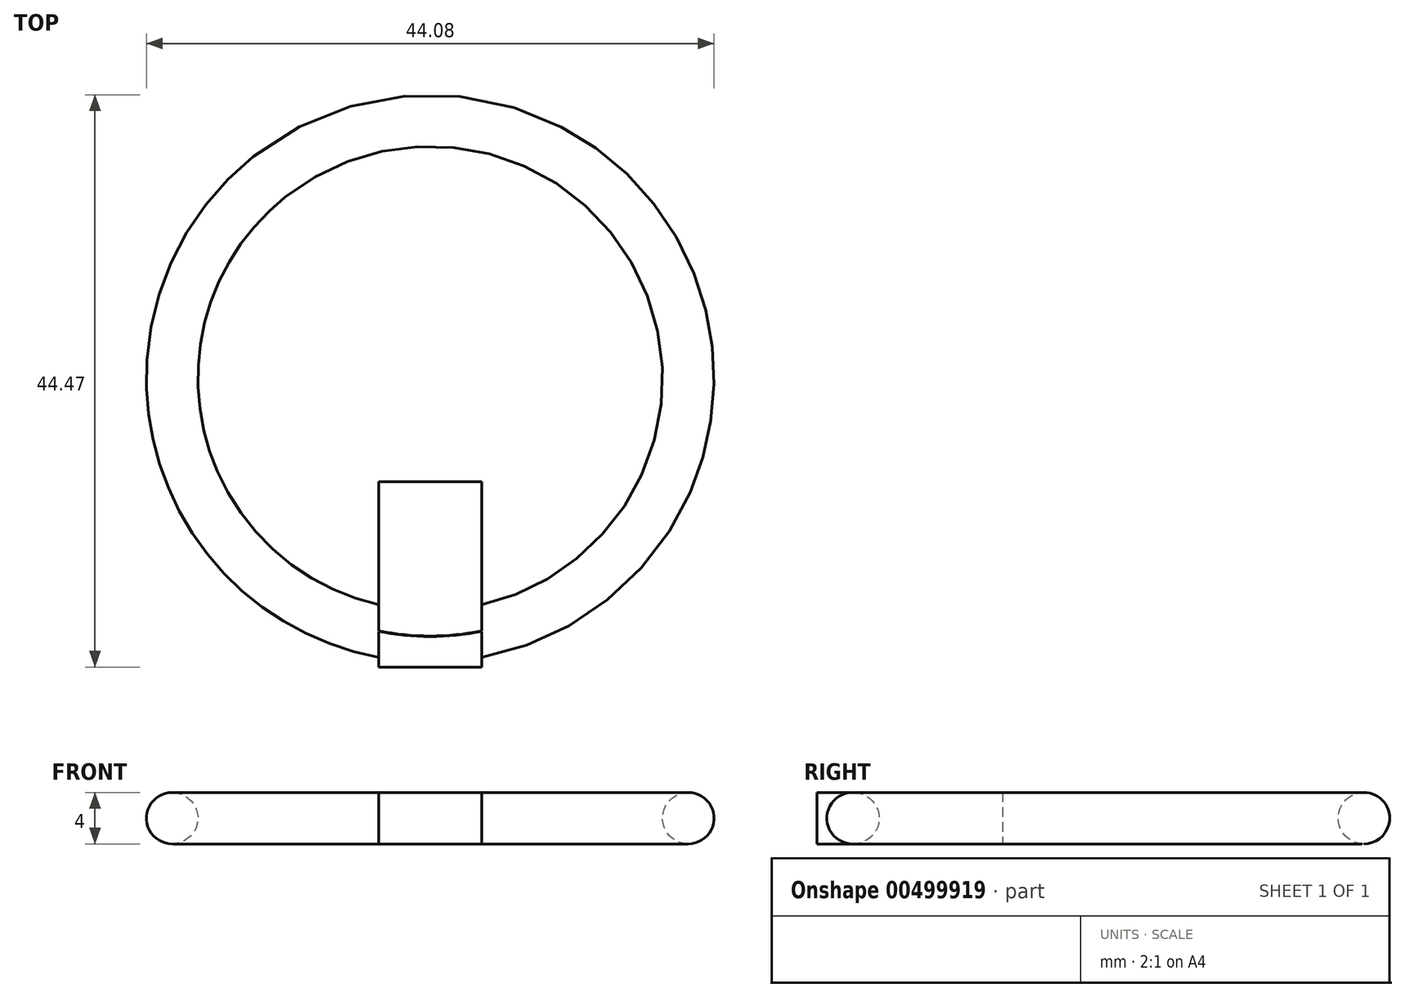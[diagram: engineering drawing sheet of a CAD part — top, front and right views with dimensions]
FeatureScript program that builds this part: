
annotation { "Feature Type Name" : "Feature", "Feature Type Description" : "" }
export const myFeature = defineFeature(function(context is Context, id is Id, definition is map)
    precondition{}
    {
        {
            var Q0;
            Q0=qCreatedBy(makeId("Top.planeOp"),FACE);
            var sketch = newSketch(context, id + "F0", { "sketchPlane" : qUnion([Q0])});
            skCircle(sketch, "E0", {"center": v(0, 0) * mm, "radius": 18 * mm});
            skSolve(sketch);
        }
        {
            var Q0;
            Q0=qCreatedBy(makeId("Front.planeOp"),FACE);
            var sketch = newSketch(context, id + "F1", { "sketchPlane" : qUnion([Q0])});
            skCircle(sketch, "E1", {"center": v(-20.04, 0) * mm, "radius": 2 * mm});
            skPoint(sketch, "E2.start.orphan", {"position": v(-18.04, 0) * mm});
            skSolve(sketch);
        }
        {
            var Q0;
            Q0=makeQuery(id+"F1.imprint","IMPRINT",FACE,{"disambiguationData":[TD([[makeQuery(id+"F1.imprint","IMPRINT",EDGE,{"derivedFrom":sQuery(id+"F1.wireOp",EDGE,"E1")}),1.0]])]});
            var Q1;
            Q1=sQuery(id+"F0.wireOp",EDGE,"E0");
            sweep(context, id + "F2", {"profiles" : qUnion([Q0]), "path" : qUnion([Q1])});
        }
        {
            var Q0;
            Q0=qCreatedBy(makeId("Top.planeOp"),FACE);
            var sketch = newSketch(context, id + "F3", { "sketchPlane" : qUnion([Q0])});
            skLineSegment(sketch, "E3", {"start": v(0, -8.03) * mm, "end": v(4, -8.03) * mm});
            skLineSegment(sketch, "E4", {"start": v(4, -8.03) * mm, "end": v(4, -19.93) * mm});
            skLineSegment(sketch, "E5.MirrorCS", {"start": v(0, -8.03) * mm, "end": v(-4, -8.03) * mm});
            skLineSegment(sketch, "E6.MirrorCS", {"start": v(-4, -8.03) * mm, "end": v(-4, -19.93) * mm});
            skPoint(sketch, "E7.orphan", {"position": v(4, -21.62) * mm});
            skPoint(sketch, "E8.orphan", {"position": v(0, -22.03) * mm});
            skPoint(sketch, "E9.orphan", {"position": v(-4, -21.62) * mm});
            skLineSegment(sketch, "E10", {"start": v(4, -19.93) * mm, "end": v(4, -22.43) * mm});
            skLineSegment(sketch, "E11", {"start": v(4, -22.43) * mm, "end": v(-4, -22.43) * mm});
            skLineSegment(sketch, "E12", {"start": v(-4, -22.43) * mm, "end": v(-4, -19.93) * mm});
            skSolve(sketch);
        }
        {
            var Q0;
            Q0 = qSketchRegion(id + "F3", true);
            extrude(context, id + "F4", {"entities" : qUnion([Q0]), "operationType" : NewBodyOperationType.ADD, "depth" : 2 * mm, "hasSecondDirection" : true, "secondDirectionOppositeDirection" : true, "secondDirectionDepth" : 2 * mm});
        }
    });
